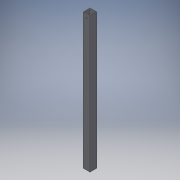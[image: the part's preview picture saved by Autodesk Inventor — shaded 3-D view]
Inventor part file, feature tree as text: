
AUTODESK INVENTOR PART (.ipt)
format: ipt  version: 2018 (Build 220112000, 112)  size: 103,424 bytes
history: native  units: in
note: dims shown in document units (in); Inventor stores cm internally (conversion verified against a paired STEP export)
features: extrude x1, shell x1, hole x1, sketch x1
ambient origin geometry x8: Origin, YZ Plane, XZ Plane, XY Plane, X Axis, Y Axis, Z Axis, Center Point
bodies: Solid1 (feature_tree)
feature tree (4):
  extrude  "Extrusion1"  Depth=1.0in
  shell  "Shell1"  Thickness=20.0in
  hole  "Hole1"  [1 undecoded]
  sketch  "Sketch1"  dims[d0=1.0in d1=1.0in d2=20.0in d3=0.0in d4=0.0625in d5=0.5in d6=0.5in d7=0.2031in d8=0.75in d9=0.375in d10=0.25in d11=0.5635in d12=1.0in d13=0.8108in]
note: 1 required parameter value undecoded (feature->parameter linkage not recoverable at this tier; creation-order binding heuristic only, values carry confidence <= 0.55)
